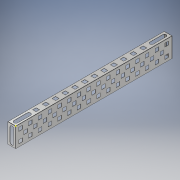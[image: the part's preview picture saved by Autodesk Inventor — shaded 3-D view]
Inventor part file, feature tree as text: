
AUTODESK INVENTOR PART (.ipt)
format: ipt  version: 2018 (Build 220112000, 112)  size: 428,032 bytes
history: native  units: in
note: dims shown in document units (in); Inventor stores cm internally (conversion verified against a paired STEP export)
features: sketch x9, extrude x8
ambient origin geometry x8: Origin, YZ Plane, XZ Plane, XY Plane, X Axis, Y Axis, Z Axis, Center Point
bodies: Solid1 (feature_tree), Solid2 (feature_tree), Solid3 (feature_tree), Solid4 (feature_tree)
feature tree (17):
  sketch  "Sketch1"  dims[d0=0.984in d1=7.874in]
  sketch  "Sketch2"  dims[d2=0.394in d3=7.874in]
  sketch  "Sketch3"  dims[d4=0.394in d5=0.984in]
  extrude  "Extrusion1"  Depth=7.874in
  extrude  "Extrusion2"  Depth=7.874in
  extrude  "Extrusion3"  Depth=0.984in
  sketch  "Sketch4"  dims[d6=0.01in d7=0.0in d8=0.01in d9=0.0in]
  extrude  "Extrusion4"  Depth=0.01in TaperAngle=0.0deg
  extrude  "Extrusion5"  Depth=0.394in
  extrude  "Extrusion6"  Depth=0.01in TaperAngle=0.0deg
  extrude  "Extrusion7"  Depth=0.01in TaperAngle=0.0deg
  extrude  "Extrusion8"  Depth=0.01in TaperAngle=0.0deg
  sketch  "Sketch5"  dims[d10=0.01in d11=0.0in d12=0.394in]
  sketch  "Sketch6"  dims[d13=0.984in d14=0.01in d15=0.0in]
  sketch  "Sketch7"  dims[d16=0.656in d17=0.01in d18=0.0in]
  sketch  "Sketch8"  dims[d19=0.656in d20=0.01in d21=0.0in]
  sketch  "Sketch9"  dims[d22=0.656in d23=0.086in d24=0.656in d25=0.1027in d26=0.1027in d28=0.1688in d29=0.3937in d31=1.0in d32=4.7244in d34=0.49in d36=0.01in d37=0.0in d38=0.1801in d39=0.18in d40=0.18in d41=0.3937in d43=1.0in d44=5.5118in d46=0.49in d48=0.3937in d50=1.0in d51=1.1811in d53=0.49in d55=0.3937in d57=1.0in d58=5.9055in d60=0.49in d62=0.01in d63=0.0in]
